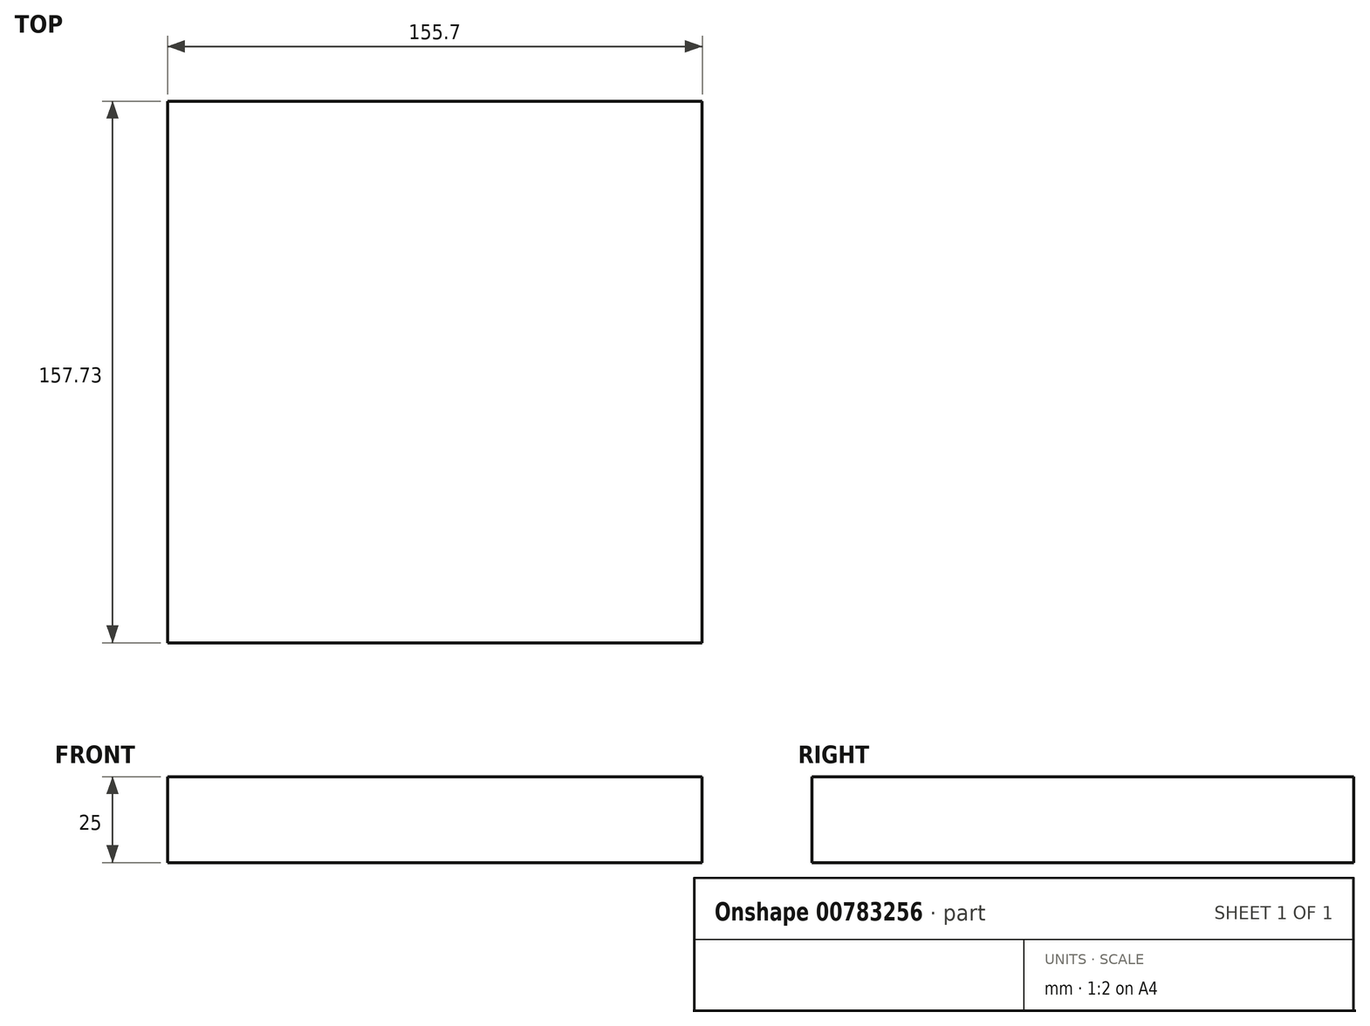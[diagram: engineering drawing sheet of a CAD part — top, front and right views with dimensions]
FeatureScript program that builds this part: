
annotation { "Feature Type Name" : "Feature", "Feature Type Description" : "" }
export const myFeature = defineFeature(function(context is Context, id is Id, definition is map)
    precondition{}
    {
        {
            var Q0;
            Q0=qCreatedBy(makeId("Top.planeOp"),FACE);
            var sketch = newSketch(context, id + "F0", { "sketchPlane" : qUnion([Q0])});
            skLineSegment(sketch, "E0.bottom", {"start": v(-69.64, -52.32) * mm, "end": v(86.06, -52.32) * mm});
            skLineSegment(sketch, "E0.top", {"start": v(-69.64, 105.4) * mm, "end": v(86.06, 105.4) * mm});
            skLineSegment(sketch, "E0.left", {"start": v(-69.64, -52.32) * mm, "end": v(-69.64, 105.4) * mm});
            skLineSegment(sketch, "E0.right", {"start": v(86.06, -52.32) * mm, "end": v(86.06, 105.4) * mm});
            skSolve(sketch);
        }
        {
            var Q0;
            Q0=makeQuery(id+"F0.imprint","IMPRINT",FACE,{"disambiguationData":[TD([[makeQuery(id+"F0.imprint","IMPRINT",EDGE,{"derivedFrom":sQuery(id+"F0.wireOp",EDGE,"E0.bottom")}),1.0]])]});
            extrude(context, id + "F1", {"entities" : qUnion([Q0]), "depth" : 25 * mm, "offsetDistance" : 25 * mm});
        }
    });
